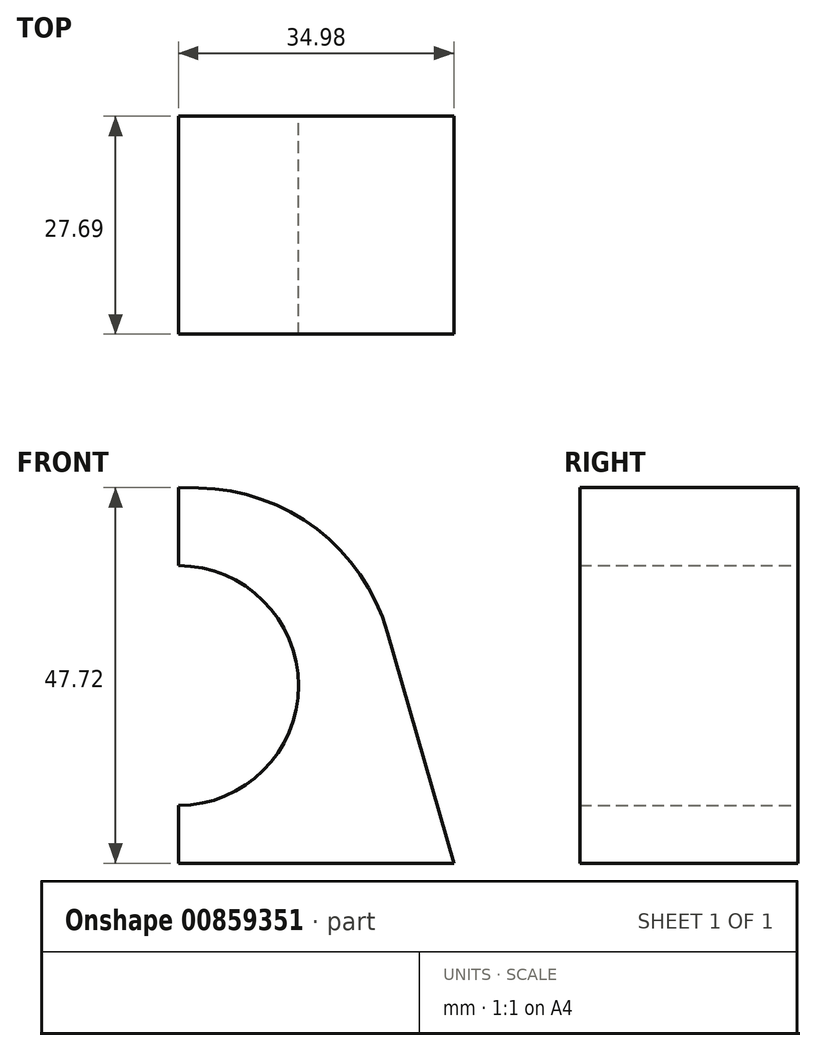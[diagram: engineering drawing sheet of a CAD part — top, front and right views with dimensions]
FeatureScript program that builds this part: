
annotation { "Feature Type Name" : "Feature", "Feature Type Description" : "" }
export const myFeature = defineFeature(function(context is Context, id is Id, definition is map)
    precondition{}
    {
        {
            var Q0;
            Q0=qCreatedBy(makeId("Front.planeOp"),FACE);
            var sketch = newSketch(context, id + "F0", { "sketchPlane" : qUnion([Q0])});
            skLineSegment(sketch, "E0", {"start": v(-34.98, 0) * mm, "end": v(-34.98, 47.72) * mm});
            skLineSegment(sketch, "E1", {"start": v(-34.98, 47.72) * mm, "end": v(-32.44, 47.68) * mm});
            skLineSegment(sketch, "E2", {"start": v(-8.42, 29.3) * mm, "end": v(0, 0) * mm});
            skLineSegment(sketch, "E3", {"start": v(0, 0) * mm, "end": v(-34.98, 0) * mm});
            skCircle(sketch, "E4", {"center": v(-34.98, 22.57) * mm, "radius": 15.24 * mm});
            skPoint(sketch, "E5.visualSharp", {"position": v(-13.62, 47.4) * mm});
            skArc(sketch, "E5.filletArc", {"start": v(-8.42, 29.3) * mm, "mid": v(-17.4, 42.45) * mm, "end": v(-32.44, 47.68) * mm});
            skSolve(sketch);
        }
        {
            var Q0;
            {var subQ0=sQuery(id+"F0.wireOp",EDGE,"E1");Q0=makeQuery(id+"F0.imprint","IMPRINT",FACE,{"disambiguationData":[TD([[makeQuery(id+"F0.imprint","IMPRINT",EDGE,{"derivedFrom":subQ0}),-1.0]])]});}
            extrude(context, id + "F1", {"entities" : qUnion([Q0]), "depth" : 27.7 * mm, "offsetDistance" : 25.4 * mm});
        }
    });
